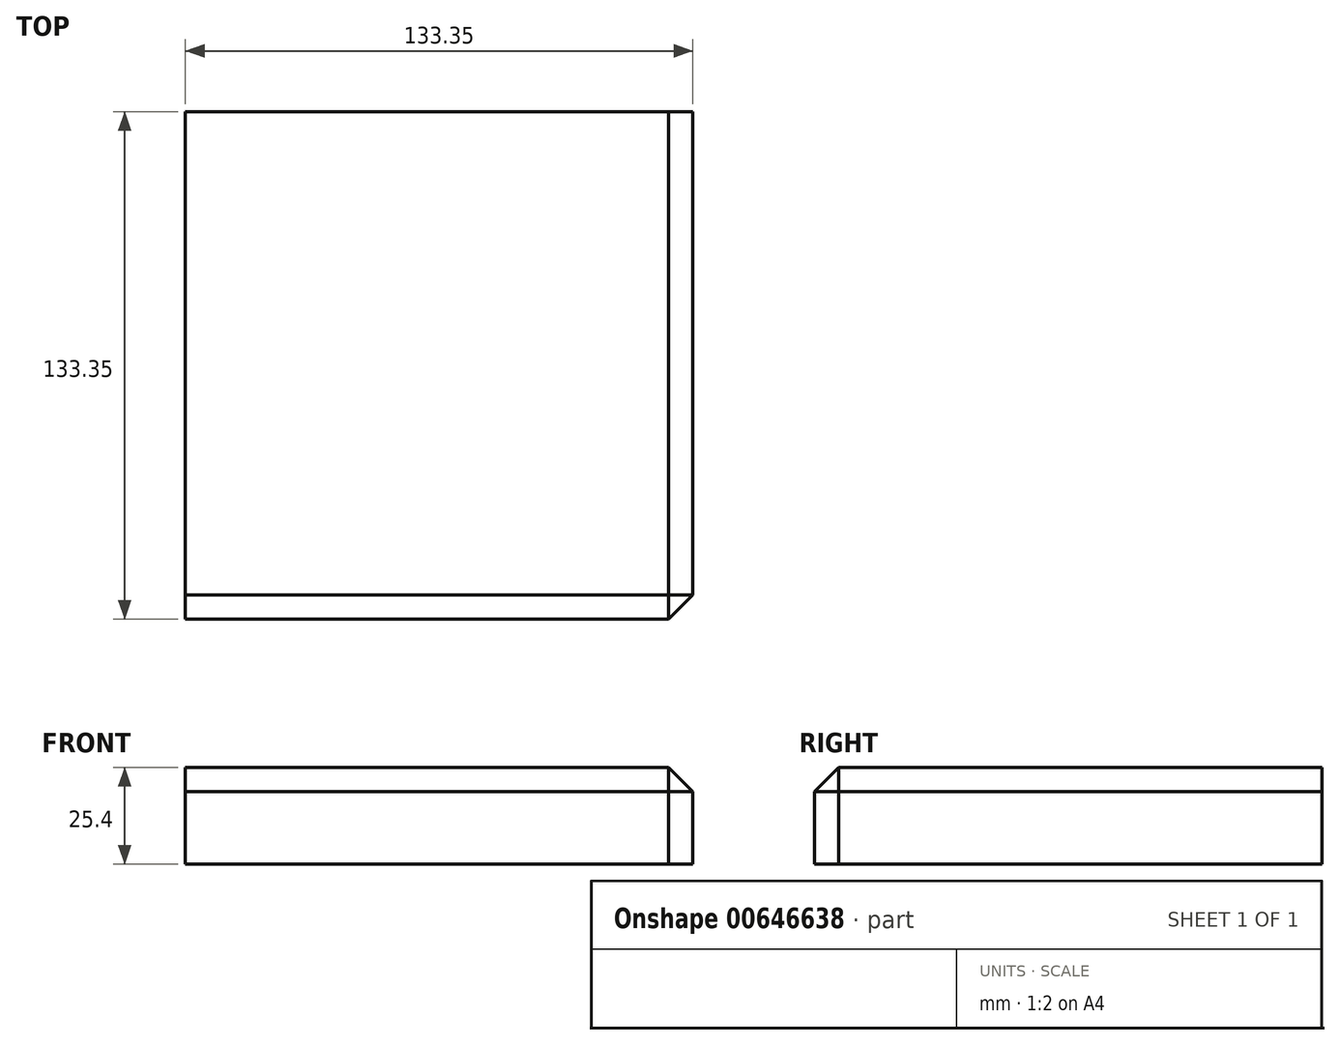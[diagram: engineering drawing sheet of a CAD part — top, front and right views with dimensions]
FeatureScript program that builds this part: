
annotation { "Feature Type Name" : "Feature", "Feature Type Description" : "" }
export const myFeature = defineFeature(function(context is Context, id is Id, definition is map)
    precondition{}
    {
        {
            var Q0;
            Q0=qCreatedBy(makeId("Top.planeOp"),FACE);
            var sketch = newSketch(context, id + "F0", { "sketchPlane" : qUnion([Q0])});
            skLineSegment(sketch, "E0.bottom", {"start": v(0, 0) * mm, "end": v(133.35, 0) * mm});
            skLineSegment(sketch, "E0.top", {"start": v(0, 133.35) * mm, "end": v(133.35, 133.35) * mm});
            skLineSegment(sketch, "E0.left", {"start": v(0, 0) * mm, "end": v(0, 133.35) * mm});
            skLineSegment(sketch, "E0.right", {"start": v(133.35, 0) * mm, "end": v(133.35, 133.35) * mm});
            skSolve(sketch);
        }
        {
            var Q0;
            Q0=makeQuery(id+"F0.imprint","IMPRINT",FACE,{"disambiguationData":[TD([[makeQuery(id+"F0.imprint","IMPRINT",EDGE,{"derivedFrom":sQuery(id+"F0.wireOp",EDGE,"E0.bottom")}),1.0]])]});
            extrude(context, id + "F1", {"entities" : qUnion([Q0]), "depth" : 25.4 * mm, "offsetDistance" : 25.4 * mm});
        }
        {
            var Q0;
            Q0=makeQuery(id+"F1.opExtrude","CAP_EDGE",EDGE,{"disambiguationData":[OSD([sQuery(id+"F0.wireOp",EDGE,"E0.bottom")])],"isStart":false});
            var Q1;
            Q1=makeQuery(id+"F1.opExtrude","CAP_EDGE",EDGE,{"disambiguationData":[OSD([sQuery(id+"F0.wireOp",EDGE,"E0.right")])],"isStart":false});
            var Q2;
            Q2=makeQuery(id+"F1.opExtrude","SWEPT_EDGE",EDGE,{"disambiguationData":[OSD([sQuery(id+"F0.wireOp",EDGE,"E0.bottom"),sQuery(id+"F0.wireOp",EDGE,"E0.right")])]});
            chamfer(context, id + "F2", {"entities" : qUnion([Q0, Q1, Q2]), "width" : 6.35 * mm, "tangentPropagation" : true});
        }
    });
